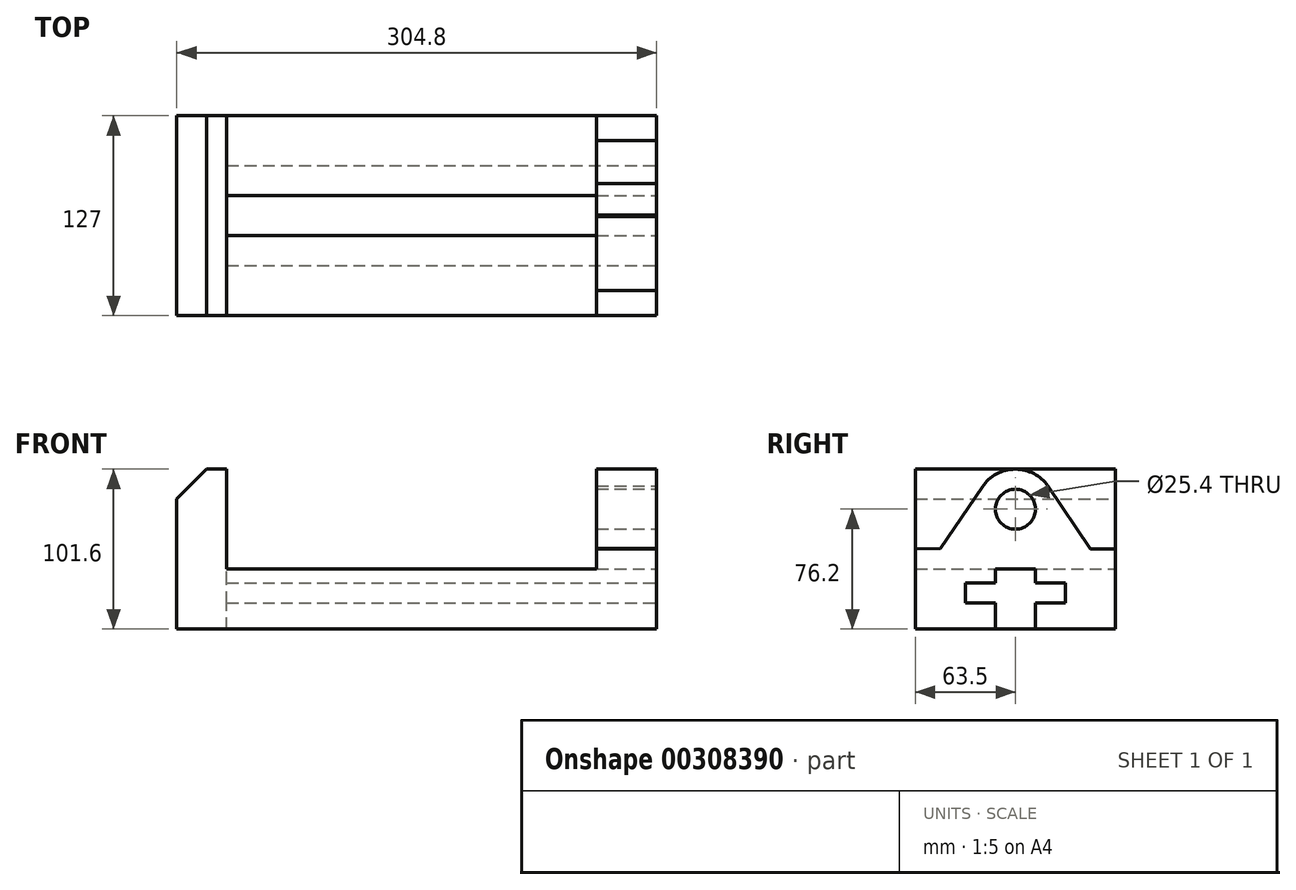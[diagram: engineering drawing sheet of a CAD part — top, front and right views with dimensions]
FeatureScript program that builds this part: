
annotation { "Feature Type Name" : "Feature", "Feature Type Description" : "" }
export const myFeature = defineFeature(function(context is Context, id is Id, definition is map)
    precondition{}
    {
        {
            var Q0;
            Q0=qCreatedBy(makeId("Front.planeOp"),FACE);
            var sketch = newSketch(context, id + "F0", { "sketchPlane" : qUnion([Q0])});
            skLineSegment(sketch, "E0", {"start": v(0, 0) * mm, "end": v(0, 101.6) * mm});
            skLineSegment(sketch, "E1", {"start": v(0, 101.6) * mm, "end": v(31.75, 101.6) * mm});
            skLineSegment(sketch, "E2", {"start": v(31.75, 101.6) * mm, "end": v(31.75, 38.1) * mm});
            skLineSegment(sketch, "E3", {"start": v(31.75, 38.1) * mm, "end": v(266.7, 38.1) * mm});
            skLineSegment(sketch, "E4", {"start": v(266.7, 38.1) * mm, "end": v(266.7, 101.6) * mm});
            skLineSegment(sketch, "E5", {"start": v(266.7, 101.6) * mm, "end": v(304.8, 101.6) * mm});
            skLineSegment(sketch, "E6", {"start": v(304.8, 101.6) * mm, "end": v(304.8, 0) * mm});
            skLineSegment(sketch, "E7", {"start": v(304.8, 0) * mm, "end": v(0, 0) * mm});
            skSolve(sketch);
        }
        {
            var Q0;
            Q0=makeQuery(id+"F0.imprint","IMPRINT",FACE,{"disambiguationData":[TD([[makeQuery(id+"F0.imprint","IMPRINT",EDGE,{"derivedFrom":sQuery(id+"F0.wireOp",EDGE,"E0")}),-1.0]])]});
            extrude(context, id + "F1", {"entities" : qUnion([Q0]), "depth" : 127 * mm});
        }
        {
            var Q0;
            Q0=makeQuery(id+"F1.opExtrude","SWEPT_EDGE",EDGE,{"disambiguationData":[OSD([sQuery(id+"F0.wireOp",EDGE,"E0"),sQuery(id+"F0.wireOp",EDGE,"E1")])]});
            chamfer(context, id + "F2", {"entities" : qUnion([Q0]), "width" : 19.05 * mm, "tangentPropagation" : true});
        }
        {
            var Q0;
            Q0=makeQuery(id+"F1.opExtrude","SWEPT_FACE",FACE,{"disambiguationData":[OSD([sQuery(id+"F0.wireOp",EDGE,"E6")])]});
            var sketch = newSketch(context, id + "F3", { "sketchPlane" : qUnion([Q0])});
            skLineSegment(sketch, "E8", {"start": v(-127, 50.8) * mm, "end": v(-127, 50.8) * mm});
            skLineSegment(sketch, "E9", {"start": v(0, 0) * mm, "end": v(-50.8, 0) * mm});
            skLineSegment(sketch, "E10", {"start": v(-50.8, 0) * mm, "end": v(-50.8, 16.5) * mm});
            skLineSegment(sketch, "E11", {"start": v(-50.8, 16.5) * mm, "end": v(-31.75, 16.5) * mm});
            skLineSegment(sketch, "E12", {"start": v(-31.75, 16.5) * mm, "end": v(-31.75, 29.21) * mm});
            skLineSegment(sketch, "E13", {"start": v(-31.75, 29.21) * mm, "end": v(-50.8, 29.21) * mm});
            skLineSegment(sketch, "E14", {"start": v(-50.8, 29.2) * mm, "end": v(-50.8, 38.1) * mm});
            skLineSegment(sketch, "E15", {"start": v(-50.8, 38.1) * mm, "end": v(-76.2, 38.1) * mm});
            skLineSegment(sketch, "E16", {"start": v(-76.2, 38.1) * mm, "end": v(-76.2, 29.21) * mm});
            skLineSegment(sketch, "E17", {"start": v(-76.2, 29.21) * mm, "end": v(-95.25, 29.21) * mm});
            skLineSegment(sketch, "E18", {"start": v(-95.25, 29.21) * mm, "end": v(-95.25, 16.5) * mm});
            skLineSegment(sketch, "E19", {"start": v(-95.25, 16.5) * mm, "end": v(-76.2, 16.51) * mm});
            skLineSegment(sketch, "E20", {"start": v(-76.2, 16.5) * mm, "end": v(-76.2, 0) * mm});
            skLineSegment(sketch, "E21", {"start": v(-76.2, 0) * mm, "end": v(-127, 0) * mm});
            skLineSegment(sketch, "E22", {"start": v(-111.13, 51.28) * mm, "end": v(-84.51, 90.47) * mm});
            skArc(sketch, "E23", {"start": v(-84.51, 90.47) * mm, "mid": v(-63.87, 101.6) * mm, "end": v(-42.92, 91.08) * mm});
            skLineSegment(sketch, "E24", {"start": v(-111.13, 51.28) * mm, "end": v(-127, 50.8) * mm});
            skLineSegment(sketch, "E25", {"start": v(-42.92, 91.08) * mm, "end": v(-15.87, 50.8) * mm});
            skLineSegment(sketch, "E26", {"start": v(-15.88, 50.8) * mm, "end": v(0, 50.8) * mm});
            skCircle(sketch, "E27", {"center": v(-63.5, 76.2) * mm, "radius": 12.7 * mm});
            skLineSegment(sketch, "E28", {"start": v(-63.13, 101.6) * mm, "end": v(-127, 101.6) * mm});
            skPoint(sketch, "E28.startSnap0", {"position": v(-63.87, 101.6) * mm});
            skLineSegment(sketch, "E29", {"start": v(-127, 101.6) * mm, "end": v(-127, 50.8) * mm});
            skLineSegment(sketch, "E30", {"start": v(-63.13, 101.6) * mm, "end": v(0, 101.6) * mm});
            skLineSegment(sketch, "E31", {"start": v(0, 101.6) * mm, "end": v(0, 50.8) * mm});
            skSolve(sketch);
        }
        {
            var Q0;
            {var subQ1=sQuery(id+"F3.wireOp",EDGE,"E22");Q0=makeQuery(id+"F3.imprint","IMPRINT",FACE,{"disambiguationData":[TD([[makeQuery(id+"F3.imprint","IMPRINT",EDGE,{"derivedFrom":subQ1}),1.0]])]});}
            var Q1;
            {var subQ1=sQuery(id+"F3.wireOp",EDGE,"E25");Q1=makeQuery(id+"F3.imprint","IMPRINT",FACE,{"disambiguationData":[TD([[makeQuery(id+"F3.imprint","IMPRINT",EDGE,{"derivedFrom":subQ1}),1.0]])]});}
            var Q2;
            Q2=makeQuery(id+"F1.opExtrude","SWEPT_FACE",FACE,{"disambiguationData":[OSD([sQuery(id+"F0.wireOp",EDGE,"E4")])]});
            extrude(context, id + "F4", {"entities" : qUnion([Q0, Q1]), "operationType" : NewBodyOperationType.REMOVE, "endBound" : BoundingType.UP_TO_SURFACE, "oppositeDirection" : true, "endBoundEntityFace" : qUnion([Q2]), "depth" : 50.8 * mm});
        }
        {
            var Q0;
            {var subQ0=sQuery(id+"F3.wireOp",EDGE,"E10");Q0=makeQuery(id+"F3.imprint","IMPRINT",FACE,{"disambiguationData":[TD([[makeQuery(id+"F3.imprint","IMPRINT",EDGE,{"derivedFrom":subQ0}),1.0]])]});}
            var Q1;
            Q1=makeQuery(id+"F1.opExtrude","SWEPT_FACE",FACE,{"disambiguationData":[OSD([sQuery(id+"F0.wireOp",EDGE,"E2")])]});
            extrude(context, id + "F5", {"entities" : qUnion([Q0]), "operationType" : NewBodyOperationType.REMOVE, "endBound" : BoundingType.UP_TO_SURFACE, "oppositeDirection" : true, "endBoundEntityFace" : qUnion([Q1]), "depth" : 25.4 * mm});
        }
        {
            var Q0;
            Q0=makeQuery(id+"F3.imprint","IMPRINT",FACE,{"disambiguationData":[TD([[makeQuery(id+"F3.imprint","IMPRINT",EDGE,{"derivedFrom":sQuery(id+"F3.wireOp",EDGE,"E27")}),1.0]])]});
            var Q1;
            Q1=makeQuery(id+"F1.opExtrude","SWEPT_FACE",FACE,{"disambiguationData":[OSD([sQuery(id+"F0.wireOp",EDGE,"E4")])]});
            extrude(context, id + "F6", {"entities" : qUnion([Q0]), "operationType" : NewBodyOperationType.REMOVE, "endBound" : BoundingType.UP_TO_SURFACE, "oppositeDirection" : true, "endBoundEntityFace" : qUnion([Q1]), "depth" : 25.4 * mm});
        }
    });
